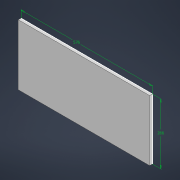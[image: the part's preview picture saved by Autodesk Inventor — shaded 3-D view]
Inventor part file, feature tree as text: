
AUTODESK INVENTOR PART (.ipt)
format: ipt  version: 2022 (Build 260153000, 153)  size: 86,016 bytes
history: native  units: mm
features: other x1, extrude x1, sketch x1
ambient origin geometry x8: Origin, YZ Plane, XZ Plane, XY Plane, X Axis, Y Axis, Z Axis, Center Point
bodies: Body1 (feature_tree)
feature tree (3):
  other  "Твердое тело1"
  extrude  "Выдавливание1"  Depth=576.0mm
  sketch  "Эскиз1"
